# Revit family: MCL-G
name_source: partatom
category: Pipe Accessories
revit_build: Autodesk Revit 2018 (Build: 20170223_1515(x64)
units: mm (PartAtom-declared; Revit-internal decimal feet)

## family parameters
Always vertical = Yes
Cut with Voids When Loaded = No
Part Type = Normal
Round Connector Dimension = Use Diameter
Shared = No
Work Plane-Based = No

## types (8) — shared parameters
Description = HYDRO MECHANICAL ECONOMY GREASE INTERCEPTOR
Manufacturer = MIFAB
URL = WWW.MIFAB.COM

## per-type parameters (varying)
| type | A-Width | B-Length | C-Pipe Offset | E-Height |
| MCL-G-0 | 1' - 4 3/4" | 0' - 11 1/4" | 0' - 2 1/2" | 0' - 11" |
| MCL-G-1 | 1' - 5 3/4" | 1' - 1 3/4" | 0' - 3 1/2" | 1' - 0" |
| MCL-G-2 | 1' - 9 1/4" | 1' - 3 3/4" | 0' - 3 1/2" | 1' - 1" |
| MCL-G-3 | 1' - 11 3/4" | 1' - 3 3/4" | 0' - 3 1/2" | 1' - 3" |
| MCL-G-4 | 1' - 11 3/4" | 1' - 3 3/4" | 0' - 3 1/2" | 1' - 5 1/2" |
| MCL-G-5 | 2' - 3 3/4" | 1' - 6 3/4" | 0' - 3 1/2" | 1' - 5 1/2" |
| MCL-G-6 | 2' - 7 1/4" | 1' - 11 3/4" | 0' - 5 1/2" | 1' - 10" |
| MCL-G-7 | 2' - 7 1/4" | 1' - 11 3/4" | 0' - 5 1/2" | 2' - 0" |

note: column(s) folded — value = type name in every type: Model

## geometry (parser evidence)
native form markers: Sweep x5
no freeform markers — native parametric forms only
